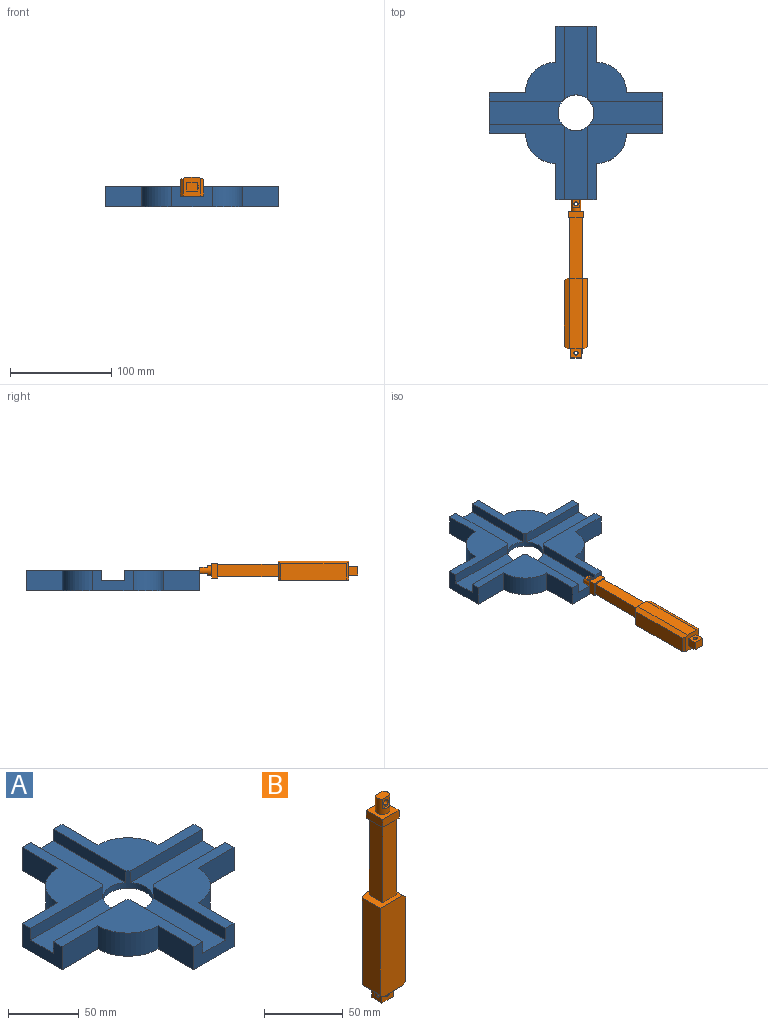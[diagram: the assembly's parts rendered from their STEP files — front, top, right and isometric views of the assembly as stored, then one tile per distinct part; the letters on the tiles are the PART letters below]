
ASSEMBLY  parts=2 mates=1
PART A: 36 faces, bbox 171.8x171.8x20 mm
  f0: plane 74.46x74.46mm, normal (0,0,1), area 1906.9mm2, adj f3,f6,f8,f9,f10,f22,f25,f33
  f1: plane 74.47x74.46mm, normal (0,0,1), area 1907.3mm2, adj f3,f4,f11,f12,f13,f24,f27,f33
  f2: plane 74.47x74.47mm, normal (0,0,1), area 1907.6mm2, adj f4,f5,f14,f15,f16,f28,f30,f33
  f3: plane 40x20mm, normal (1,0,0), area 571.4mm2, adj f0,f1,f10,f11,f20,f24,f25,f26
  f4: plane 40x20mm, normal (0,1,0), area 571.4mm2, adj f1,f2,f13,f14,f20,f27,f28,f29
  f5: plane 40x20mm, normal (-1,0,0), area 571.4mm2, adj f2,f7,f16,f17,f20,f30,f31,f32
  f6: plane 40x20mm, normal (0,-1,0), area 571.4mm2, adj f0,f7,f8,f19,f20,f21,f22,f23
  f7: plane 74.47x74.46mm, normal (0,0,1), area 1907.2mm2, adj f5,f6,f17,f18,f19,f21,f31,f33
  f8: plane 35.89x20mm, normal (1,0,0), area 717.9mm2, adj f0,f6,f9,f20
  f9: cylinder r=30mm len=30mm, axis (0,0,-1), area 942.5mm2, adj f0,f8,f10,f20
  f10: plane 35.89x20mm, normal (0,-1,0), area 717.9mm2, adj f0,f3,f9,f20
  f11: plane 35.89x20mm, normal (0,1,0), area 717.9mm2, adj f1,f3,f12,f20
  f12: cylinder r=30mm len=30mm, axis (0,0,-1), area 942.5mm2, adj f1,f11,f13,f20
  f13: plane 35.89x20mm, normal (1,0,0), area 717.9mm2, adj f1,f4,f12,f20
  f14: plane 35.89x20mm, normal (-1,0,0), area 717.9mm2, adj f2,f4,f15,f20
  f15: cylinder r=30mm len=30mm, axis (0,0,-1), area 942.5mm2, adj f2,f14,f16,f20
  f16: plane 35.89x20mm, normal (0,1,0), area 717.9mm2, adj f2,f5,f15,f20
  f17: plane 35.89x20mm, normal (0,-1,0), area 717.9mm2, adj f5,f7,f18,f20
  f18: cylinder r=30mm len=30mm, axis (0,0,-1), area 942.5mm2, adj f7,f17,f19,f20
  f19: plane 35.89x20mm, normal (-1,0,0), area 717.9mm2, adj f6,f7,f18,f20
  f20: plane 171.79x171.79mm, normal (0,0,-1), area 9210mm2, adj f3,f4,f5,f6,f8,f9,f10,f11
  f21: plane 72.32x10mm, normal (1,0,0), area 723.2mm2, adj f6,f7,f23,f33
  f22: plane 72.32x10mm, normal (-1,0,0), area 723.2mm2, adj f0,f6,f23,f33
  f23: plane 72.32x22.86mm, normal (0,0,1), area 1588mm2, adj f6,f21,f22,f33
  f24: plane 72.31x10mm, normal (0,-1,0), area 723.1mm2, adj f1,f3,f26,f33
  f25: plane 72.32x10mm, normal (0,1,0), area 723.2mm2, adj f0,f3,f26,f33
  f26: plane 72.32x22.86mm, normal (0,0,1), area 1587.9mm2, adj f3,f24,f25,f33
  f27: plane 72.31x10mm, normal (-1,0,0), area 723.1mm2, adj f1,f4,f29,f33
  f28: plane 72.31x10mm, normal (1,0,0), area 723.1mm2, adj f2,f4,f29,f33
  f29: plane 72.31x22.86mm, normal (0,0,1), area 1587.8mm2, adj f4,f27,f28,f33
  f30: plane 72.31x10mm, normal (0,-1,0), area 723.1mm2, adj f2,f5,f32,f33
  f31: plane 72.32x10mm, normal (0,1,0), area 723.2mm2, adj f5,f7,f32,f33
  f32: plane 72.32x22.86mm, normal (0,0,1), area 1587.9mm2, adj f5,f30,f31,f33
  f33: cylinder r=17.75mm len=35.5mm, axis (0,0,1), area 679.4mm2, adj f0,f1,f2,f7,f21,f22,f23,f24
  f34: cylinder r=42.82mm len=85.64mm, axis (0,0,1), area 1345.2mm2, adj f20,f35
  f35: plane 85.64x85.64mm, normal (0,0,-1), area 4770.6mm2, adj f33,f34
PART B: 38 faces, bbox 22.9x18.8x156.5 mm
  f0: cylinder r=2.03mm len=6.1mm, axis (0,-1,0), area 77.8mm2, adj f31,f33
  f1: cylinder r=2.03mm len=8.89mm, axis (0,-1,0), area 113.5mm2, adj f6,f8
  f2: cylinder r=4.59mm len=11.68mm, axis (0,0,-1), area 222.6mm2, adj f28,f29,f30,f31,f32,f33
  f3: plane 18.8x17.78mm, normal (0,0,-1), area 236.2mm2, adj f5,f6,f7,f8,f11,f13,f14,f15
  f4: plane 20.32x18.8mm, normal (0,0,1), area 228.3mm2, adj f11,f12,f13,f14,f15,f18,f19,f20
  f5: plane 9.14x8.89mm, normal (1,0,0), area 81.3mm2, adj f3,f6,f8,f9
  f6: plane 10.16x9.14mm, normal (0,1,0), area 79.9mm2, adj f1,f3,f5,f7,f9
  f7: plane 9.14x8.89mm, normal (-1,0,0), area 68.4mm2, adj f3,f6,f8,f9,f34,f36,f37
  f8: plane 10.16x9.14mm, normal (0,-1,0), area 79.9mm2, adj f1,f3,f5,f7,f9
  f9: plane 10.16x8.89mm, normal (0,0,-1), area 90.3mm2, adj f5,f6,f7,f8
  f10: plane 64.77x16.26mm, normal (1,0,0), area 1052.9mm2, adj f13,f15,f17,f18
  f11: plane 69.85x12.7mm, normal (0,1,0), area 887.1mm2, adj f3,f4,f14,f15
  f12: plane 67.31x16.26mm, normal (-1,0,0), area 1094.2mm2, adj f4,f13,f14,f16
  f13: plane 69.85x22.86mm, normal (0,-1,0), area 1587.1mm2, adj f3,f4,f10,f12,f16,f17,f18
  f14: plane 69.85x5.08mm, normal (-0.45,0.89,0), area 393.1mm2, adj f3,f4,f11,f12,f16
  f15: plane 69.85x5.08mm, normal (0.45,0.89,0), area 389.5mm2, adj f3,f4,f10,f11,f17,f18
  f16: plane 17.53x2.54mm, normal (-0.71,0,-0.71), area 60.7mm2, adj f3,f12,f13,f14
  f17: plane 17.53x2.54mm, normal (0.71,0,-0.71), area 60.7mm2, adj f3,f10,f13,f15
  f18: plane 17.53x2.54mm, normal (0.71,0,0.71), area 60.7mm2, adj f4,f10,f13,f15
  f19: plane 59.69x12.07mm, normal (1,0,0), area 720.2mm2, adj f4,f20,f22,f23
  f20: plane 59.69x12.07mm, normal (0,1,0), area 720.2mm2, adj f4,f19,f21,f23
  f21: plane 59.69x12.07mm, normal (-1,0,0), area 720.2mm2, adj f4,f20,f22,f23
  f22: plane 59.69x12.07mm, normal (0,-1,0), area 720.2mm2, adj f4,f19,f21,f23
  f23: plane 14.73x14.73mm, normal (0,0,-1), area 71.5mm2, adj f19,f20,f21,f22,f24,f25,f26,f27
  f24: plane 14.73x6.1mm, normal (1,0,0), area 89.8mm2, adj f23,f25,f27,f28
  f25: plane 14.73x6.1mm, normal (0,1,0), area 89.8mm2, adj f23,f24,f26,f28
  f26: plane 14.73x6.1mm, normal (-1,0,0), area 89.8mm2, adj f23,f25,f27,f28
  f27: plane 14.73x6.1mm, normal (0,-1,0), area 89.8mm2, adj f23,f24,f26,f28
  f28: plane 14.73x14.73mm, normal (0,0,1), area 151mm2, adj f2,f24,f25,f26,f27
  f29: plane 9.17x6.1mm, normal (0,0,1), area 51.5mm2, adj f2,f31,f33
  f30: plane 6.85x1.54mm, normal (0,0,1), area 7.3mm2, adj f2,f31
  f31: plane 7.37x6.85mm, normal (0,-1,0), area 37.5mm2, adj f0,f2,f29,f30
  f32: plane 6.85x1.54mm, normal (0,0,1), area 7.3mm2, adj f2,f33
  f33: plane 7.37x6.85mm, normal (0,1,0), area 37.5mm2, adj f0,f2,f29,f32
  f34: cylinder r=0.64mm len=5.08mm, axis (0,0,1), area 10.1mm2, adj f3,f7,f35,f37
  f35: plane 5.08x2.54mm, normal (-1,0,0), area 12.9mm2, adj f3,f34,f36,f37
  f36: cylinder r=0.64mm len=5.08mm, axis (0,0,1), area 10.1mm2, adj f3,f7,f35,f37
  f37: plane 3.81x1.27mm, normal (0,0,-1), area 4.5mm2, adj f7,f34,f35,f36
PLACE A t=(54.64,-157.28,80.09)mm
PLACE B rot(axis=(0,0.71,0.71),180deg) t=(52.9,-409.59,100.25)mm
MATE slider B.f2 <-> A.f6  axis (0,1,0) through (52.9,-253.13,100.25)mm
